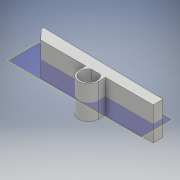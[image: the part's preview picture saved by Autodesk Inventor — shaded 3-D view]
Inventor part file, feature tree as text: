
AUTODESK INVENTOR PART (.ipt)
format: ipt  version: 2018 (Build 220112000, 112)  size: 177,152 bytes
history: native  units: mm
features: extrude x6, sketch x5, projected_geometry x2, plane x1, mirror x1
ambient origin geometry x8: Origin, YZ Plane, XZ Plane, XY Plane, X Axis, Y Axis, Z Axis, Center Point
bodies: Solid1 (feature_tree)
feature tree (15):
  sketch  "Sketch1"  dims[d1=6.1mm d3=20.0mm]
  extrude  "Extrusion1"  Depth=20.0mm
  extrude  "Extrusion2"  Depth=1.0mm
  extrude  "Extrusion3"  Depth=10.0mm TaperAngle=0.0deg
  extrude  "Extrusion4"  Depth=5.0mm
  plane  "Work Plane1"
  mirror  "Mirror1"
  extrude  "Extrusion5"  Depth=10.0mm TaperAngle=0.0deg
  extrude  "Extrusion6"  Depth=1.0mm TaperAngle=0.0deg
  sketch  "Sketch3"  dims[d4=1.0mm d5=20.0mm]
  sketch  "Sketch4"  dims[d6=10.0mm d7=0.0mm d8=10.0mm d9=0.0mm]
  sketch  "Sketch5"  dims[d10=135.0deg d11=5.0mm]
  projected_geometry  "Projected Loop1"
  sketch  "Sketch6"  dims[d12=1.0mm d13=10.0mm d14=0.0mm d15=1.0mm d16=0.0mm d17=10.0mm d18=0.0mm d19=10.0mm d20=0.0mm]
  projected_geometry  "Projected Loop2"
